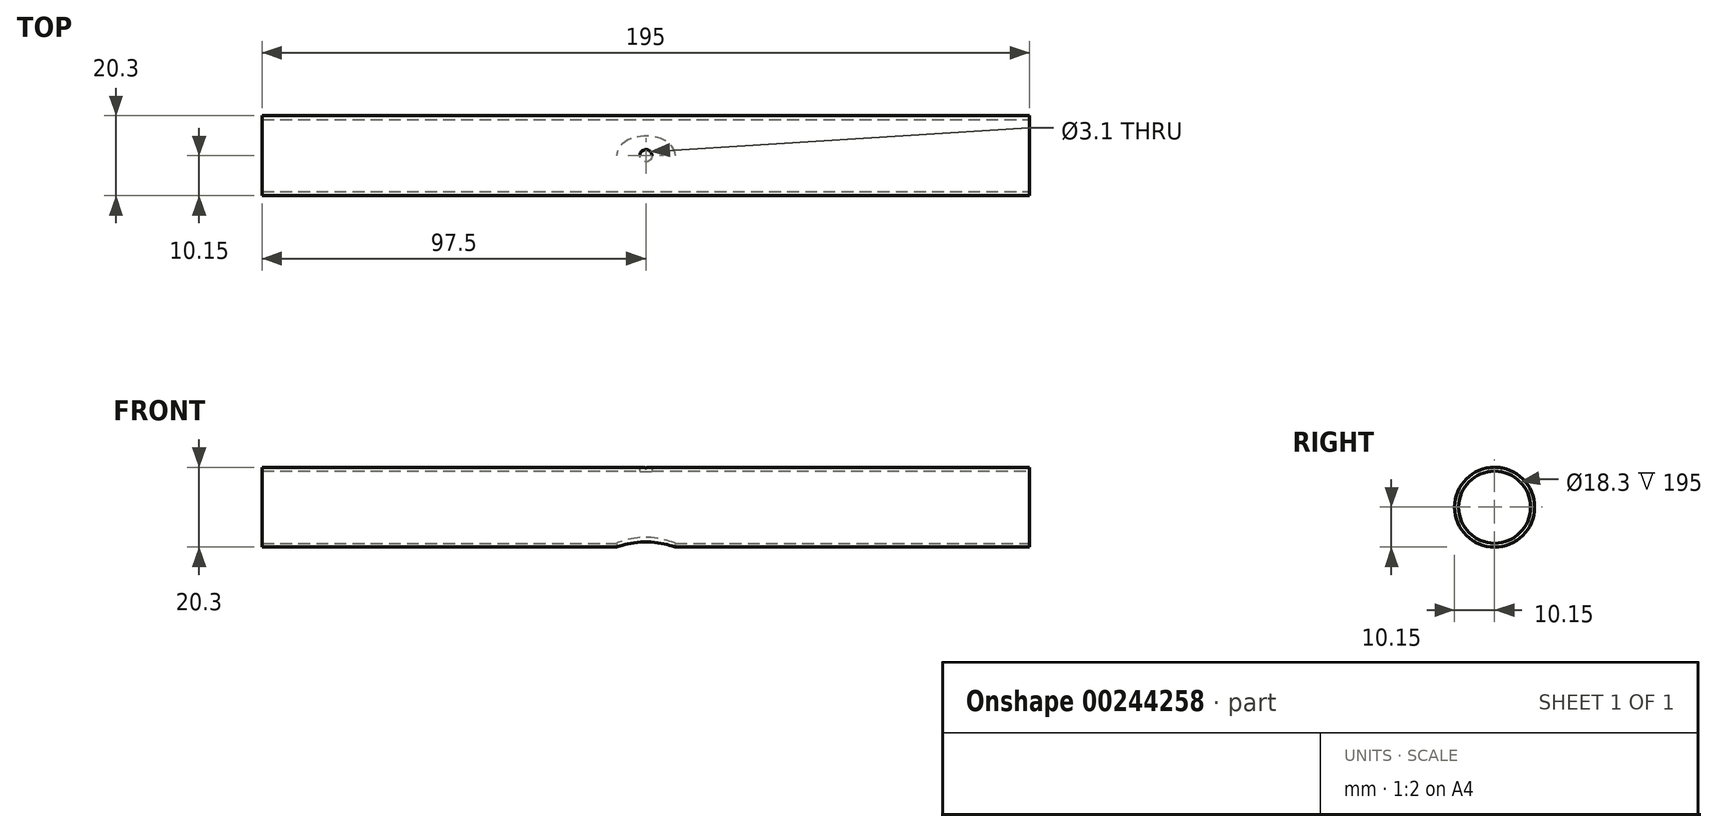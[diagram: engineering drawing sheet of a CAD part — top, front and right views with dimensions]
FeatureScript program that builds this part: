
annotation { "Feature Type Name" : "Feature", "Feature Type Description" : "" }
export const myFeature = defineFeature(function(context is Context, id is Id, definition is map)
    precondition{}
    {
        {
            var Q0;
            Q0=qCreatedBy(makeId("Right.planeOp"),FACE);
            var sketch = newSketch(context, id + "F0", { "sketchPlane" : qUnion([Q0])});
            skCircle(sketch, "E0", {"center": v(0, 0) * mm, "radius": 10.15 * mm});
            skSolve(sketch);
        }
        {
            var Q0;
            Q0=qSketchRegion(id+"F0",true);
            extrude(context, id + "F1", {"entities" : qUnion([Q0]), "depth" : 195 * mm});
        }
        {
            var Q0;
            Q0=makeQuery(id+"F1.opExtrude","CAP_FACE",FACE,{"disambiguationData":[OSD([sQuery(id+"F0.wireOp",EDGE,"E0")])],"isStart":false});
            var sketch = newSketch(context, id + "F2", { "sketchPlane" : qUnion([Q0])});
            skCircle(sketch, "E1", {"center": v(0, 0) * mm, "radius": 9.15 * mm});
            skSolve(sketch);
        }
        {
            var Q0;
            Q0=qSketchRegion(id+"F2",true);
            extrude(context, id + "F3", {"entities" : qUnion([Q0]), "operationType" : NewBodyOperationType.REMOVE, "endBound" : BoundingType.THROUGH_ALL, "oppositeDirection" : true, "depth" : 25 * mm});
        }
        {
            var Q0;
            Q0=qCreatedBy(makeId("Top.planeOp"),FACE);
            var sketch = newSketch(context, id + "F4", { "sketchPlane" : qUnion([Q0])});
            skLineSegment(sketch, "E2", {"start": v(0, 0) * mm, "end": v(195, 0) * mm, "construction": true});
            skEllipse(sketch, "E3", {"center": v(97.5, 0) * mm, "majorRadius": 7.5 * mm, "minorRadius": 5 * mm, "majorAxis": v(1, 0)});
            skSolve(sketch);
        }
        {
            var Q0;
            Q0=qSketchRegion(id+"F4",true);
            extrude(context, id + "F5", {"entities" : qUnion([Q0]), "operationType" : NewBodyOperationType.REMOVE, "endBound" : BoundingType.THROUGH_ALL, "oppositeDirection" : true, "depth" : 25 * mm});
        }
        {
            var Q0;
            Q0=qCreatedBy(makeId("Top.planeOp"),FACE);
            var sketch = newSketch(context, id + "F6", { "sketchPlane" : qUnion([Q0])});
            skLineSegment(sketch, "E4", {"start": v(0, 0) * mm, "end": v(195, 0) * mm, "construction": true});
            skCircle(sketch, "E5", {"center": v(97.5, 0) * mm, "radius": 1.55 * mm});
            skSolve(sketch);
        }
        {
            var Q0;
            Q0=qSketchRegion(id+"F6",true);
            extrude(context, id + "F7", {"entities" : qUnion([Q0]), "operationType" : NewBodyOperationType.REMOVE, "endBound" : BoundingType.THROUGH_ALL, "depth" : 25 * mm});
        }
    });
